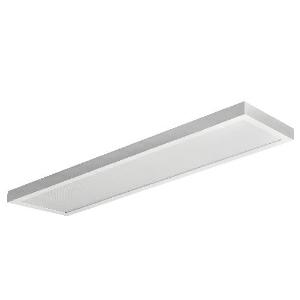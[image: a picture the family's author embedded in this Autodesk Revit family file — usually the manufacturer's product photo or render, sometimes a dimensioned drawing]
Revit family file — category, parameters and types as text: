
# Revit family: ledpanels-sf-p_l15-50w-ble2-830_840_542003156400_32c2
name_source: partatom
category: Lighting Fixtures
units: mm (PartAtom-declared; Revit-internal decimal feet)

## family parameters
Cut with Voids When Loaded = No
Host = Face
Light Source = No
Part Type = Normal
Room Calculation Point = No
Round Connector Dimension = Use Diameter
Shared = No

## types (1)
- LEDPanelS-Sf-P L15-50W-BLE2-830/840 (1 x LED, 6250 lm, 4000)
    Apparent Load = 50 VA
    Approval mark = CE, ENEC
    CIE Flux Codes = 60 87 97 100 100
    Color Rendering = 80
    Color Temperature = 4000
    Control Gear = Electronic ballast
    Default Elevation = 1800 mm
    Description = Panel Performer Surface Mounted 1574x370mm-50W-6250lm-3/4000K-Bluetooth
    Frequency = 60 Hz
    Height = 55 mm
    Lamp = 1 x LED
    Lamp Light Flux = 6250 lm
    Lamp count = 1
    Length = 1574 mm
    Luminous efficacy = 125 lm/W
    Manufacturer = OPPLE
    ModVariant = No
    Model = 542003156400
    Mounting Place = Ceiling
    Mounting Type = Surface mounted
    Number of Poles = 1
    OnlyDefault = Yes
    Power Factor = 1
    Product Name = LEDPanelS-Sf-P L15-50W-BLE2-830/840
    Product group = Ceiling mounted luminaire
    ProductGroupID = 3
    Protection Class = Safety extra-low voltage
    Protection Degree = IP 20
    RLX_Detail_Level = 1
    RLX_Emergency_Light_Flux = 0 lm
    RLX_Emergency_Type = 0
    RLX_Emergency_Type_DB = No
    RlxData = <blob elided: 100853 chars, md5=054b2db4>
    Socket = socket
    Standby Power = 0 W
    System Light Flux = 6250 lm
    System Power = 50 W
    Type Comments = Product without accessories
    Type Image = web_surface_pl.jpg
    URL = http://relux.com
    VarID = ---
    Voltage = 230 V
    Voltage Range = 220-240 V
    Weight = 0.00 kg
    Width = 370 mm

## geometry (parser evidence)
native form markers: Blend x4, Sweep x10
no freeform markers — native parametric forms only
